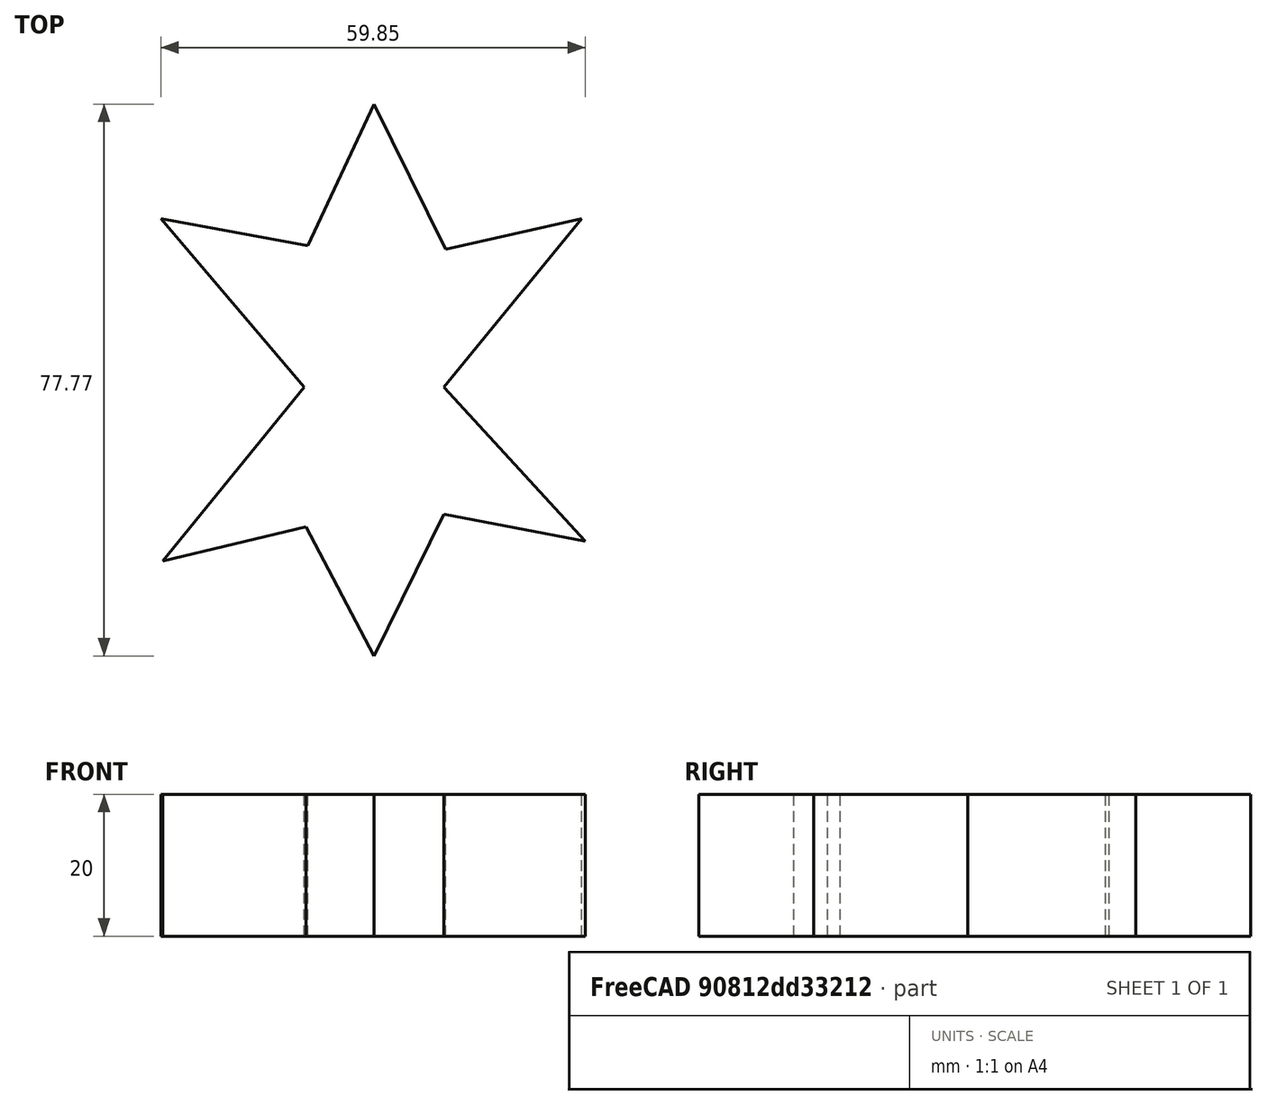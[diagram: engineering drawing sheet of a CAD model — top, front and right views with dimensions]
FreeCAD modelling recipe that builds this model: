
FCSTD DOCUMENT  (FreeCAD 0.21R33694 (Git))
Label: OJT1_T15P01_estrella_
License: All rights reserved
LicenseURL: http://en.wikipedia.org/wiki/All_rights_reserved
objects: Sketcher::SketchObject×1, PartDesign::Pad×1, PartDesign::Body×1
note: 4 computed .brp shape members not serialized (recipe doc carries the construction recipe); baked Part::Feature solids carry a one-line shape summary decoded from their .brp

FEATURE [Sketcher::SketchObject] Sketch  label="boceto"
  FullyConstrained = false
  MapMode = 5
  Support = -> [XY_Plane]
  sketch-geometry (12):
    g0: LineSegment StartX=0 StartY=49.4949 StartZ=0 EndX=10.101 EndY=29.0404 EndZ=0
    g1: LineSegment StartX=10.101 StartY=29.0404 StartZ=0 EndX=29.2929 EndY=33.3333 EndZ=0
    g2: LineSegment StartX=29.2929 StartY=33.3333 StartZ=0 EndX=9.84849 EndY=9.59596 EndZ=0
    g3: LineSegment StartX=9.84849 StartY=9.59596 StartZ=0 EndX=29.798 EndY=-12.1212 EndZ=0
    g4: LineSegment StartX=29.798 StartY=-12.1212 StartZ=0 EndX=9.84849 EndY=-8.33333 EndZ=0
    g5: LineSegment StartX=9.84849 StartY=-8.33333 StartZ=0 EndX=0 EndY=-28.2828 EndZ=0
    g6: LineSegment StartX=0 StartY=-28.2828 StartZ=0 EndX=-9.59596 EndY=-10.101 EndZ=0
    g7: LineSegment StartX=-9.59596 StartY=-10.101 StartZ=0 EndX=-29.798 EndY=-14.899 EndZ=0
    g8: LineSegment StartX=-29.798 StartY=-14.899 StartZ=0 EndX=-9.84848 EndY=9.59596 EndZ=0
    g9: LineSegment StartX=-9.84848 StartY=9.59596 StartZ=0 EndX=-30.0505 EndY=33.3333 EndZ=0
    g10: LineSegment StartX=-30.0505 StartY=33.3333 StartZ=0 EndX=-9.34343 EndY=29.5454 EndZ=0
    g11: LineSegment StartX=0 StartY=49.4949 StartZ=0 EndX=-9.34343 EndY=29.5454 EndZ=0
  constraints (14):
    c: PointOnObject(g0,g-2)
    c: Coincident(g0,g1)
    c: Coincident(g1,g2)
    c: Coincident(g2,g3)
    c: Coincident(g3,g4)
    c: Coincident(g4,g5)
    c: PointOnObject(g5,g-2)
    c: Coincident(g5,g6)
    c: Coincident(g6,g7)
    c: Coincident(g7,g8)
    c: Coincident(g8,g9)
    c: Coincident(g9,g10)
    c: Coincident(g0,g11)
    c: Coincident(g11,g10)
FEATURE [PartDesign::Pad] Pad
  Direction = (0,0,1)
  Length = 20
  Length2 = 10
  Profile = -> Sketch
  ReferenceAxis = -> Sketch [N_Axis]
  Type = 0
FEATURE [PartDesign::Body] Body  label="estrella"
  Group = -> [Sketch,Pad]
  Origin = -> Origin
  Tip = -> Pad
